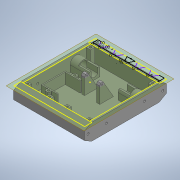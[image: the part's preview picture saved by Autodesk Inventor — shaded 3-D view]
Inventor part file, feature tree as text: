
AUTODESK INVENTOR PART (.ipt)
format: ipt  version: 2020 (Build 240168000, 168)  size: 514,048 bytes
history: native  units: in
note: dims shown in document units (in); Inventor stores cm internally (conversion verified against a paired STEP export)
features: projected_geometry x16, sketch x15, extrude x14, mirror x4, plane x2
ambient origin geometry x8: Origin, YZ Plane, XZ Plane, XY Plane, X Axis, Y Axis, Z Axis, Center Point
bodies: Solid1 (feature_tree)
feature tree (51):
  extrude  "Extrusion1"  Depth=5.9055in
  extrude  "Extrusion2"  TaperAngle=0.0deg  [1 undecoded]
  extrude  "Extrusion3"  Depth=1.063in
  extrude  "Extrusion4"  Depth=0.315in
  extrude  "Extrusion5"  TaperAngle=0.0deg  [1 undecoded]
  extrude  "Extrusion6"  Depth=0.5906in
  mirror  "Mirror1"
  extrude  "Extrusion7"  Depth=0.0787in
  mirror  "Mirror2"
  extrude  "Extrusion8"  Depth=0.6102in
  mirror  "Mirror3"
  plane  "Work Plane1"
  extrude  "Extrusion9"  Depth=0.7874in TaperAngle=0.0deg
  mirror  "Mirror4"
  extrude  "Extrusion10"  Depth=6.063in TaperAngle=0.0deg
  extrude  "Extrusion11"  Depth=0.1575in
  extrude  "Extrusion12"  TaperAngle=0.0deg  [1 undecoded]
  extrude  "Extrusion13"  Depth=0.2756in
  extrude  "Extrusion14"  Depth=0.4331in
  plane  "Work Plane2"
  sketch  "Sketch18"  dims[d34=0.122in d38=2.7559in d40=0.061in d41=0.0909in d42=0.2362in d43=0.0in d44=60.0deg d45=0.0787in d46=0.315in d48=0.993in d49=0.0in d51=0.1575in d52=0.1575in d53=0.2756in d54=0.0in d55=0.4724in d56=1.1614in d57=1.5748in d58=1.5945in d59=0.0787in d60=0.0787in d62=0.315in d63=0.7677in d64=0.0in d65=0.1575in d66=0.1575in d67=0.2756in d68=0.0in d69=0.8268in d70=0.2953in d71=0.0394in d72=0.0in d76=0.1575in d77=120.0deg d78=120.0deg d79=0.1969in d80=0.1969in d81=0.1969in d82=0.1969in d83=0.1969in]
  sketch  "Sketch1"  dims[d0=1.1811in d1=5.9055in]
  sketch  "Sketch2"  dims[d2=5.1181in d3=0.0in]
  projected_geometry  "Projected Loop1"
  sketch  "Sketch3"  dims[d4=0.1575in d5=1.063in]
  projected_geometry  "Projected Loop2"
  projected_geometry  "Projected Loop3"
  sketch  "Sketch4"  dims[d6=0.0in d8=0.315in]
  sketch  "Sketch5"  dims[d10=0.993in d11=0.0in]
  projected_geometry  "Projected Loop4"
  sketch  "Sketch6"  dims[d12=0.6496in d13=0.5906in]
  sketch  "Sketch7"  dims[d14=1.5748in d15=0.0787in]
  sketch  "Sketch9"  dims[d16=0.5512in d17=0.0in d18=0.6102in]
  sketch  "Sketch10"  dims[d19=0.4803in d20=0.7874in d21=0.0in]
  sketch  "Sketch12"  dims[d22=0.1654in d23=6.063in d24=0.0in]
  projected_geometry  "Projected Loop6"
  projected_geometry  "Projected Loop7"
  projected_geometry  "Projected Loop8"
  sketch  "Sketch13"  dims[d25=0.5114in d26=0.1575in]
  projected_geometry  "Projected Loop9"
  projected_geometry  "Projected Loop10"
  projected_geometry  "Projected Loop11"
  projected_geometry  "Projected Loop12"
  projected_geometry  "Projected Loop13"
  projected_geometry  "Projected Loop14"
  sketch  "Sketch14"  dims[d27=1.5748in d28=0.0in d29=0.0in]
  sketch  "Sketch15"  dims[d30=0.1575in d31=0.2756in]
  projected_geometry  "Projected Loop15"
  sketch  "Sketch16"  dims[d32=0.0in d33=0.4331in]
  projected_geometry  "Projected Loop17"
  projected_geometry  "Projected Loop18"
note: 3 required parameter values undecoded (feature->parameter linkage not recoverable at this tier; creation-order binding heuristic only, values carry confidence <= 0.55)
